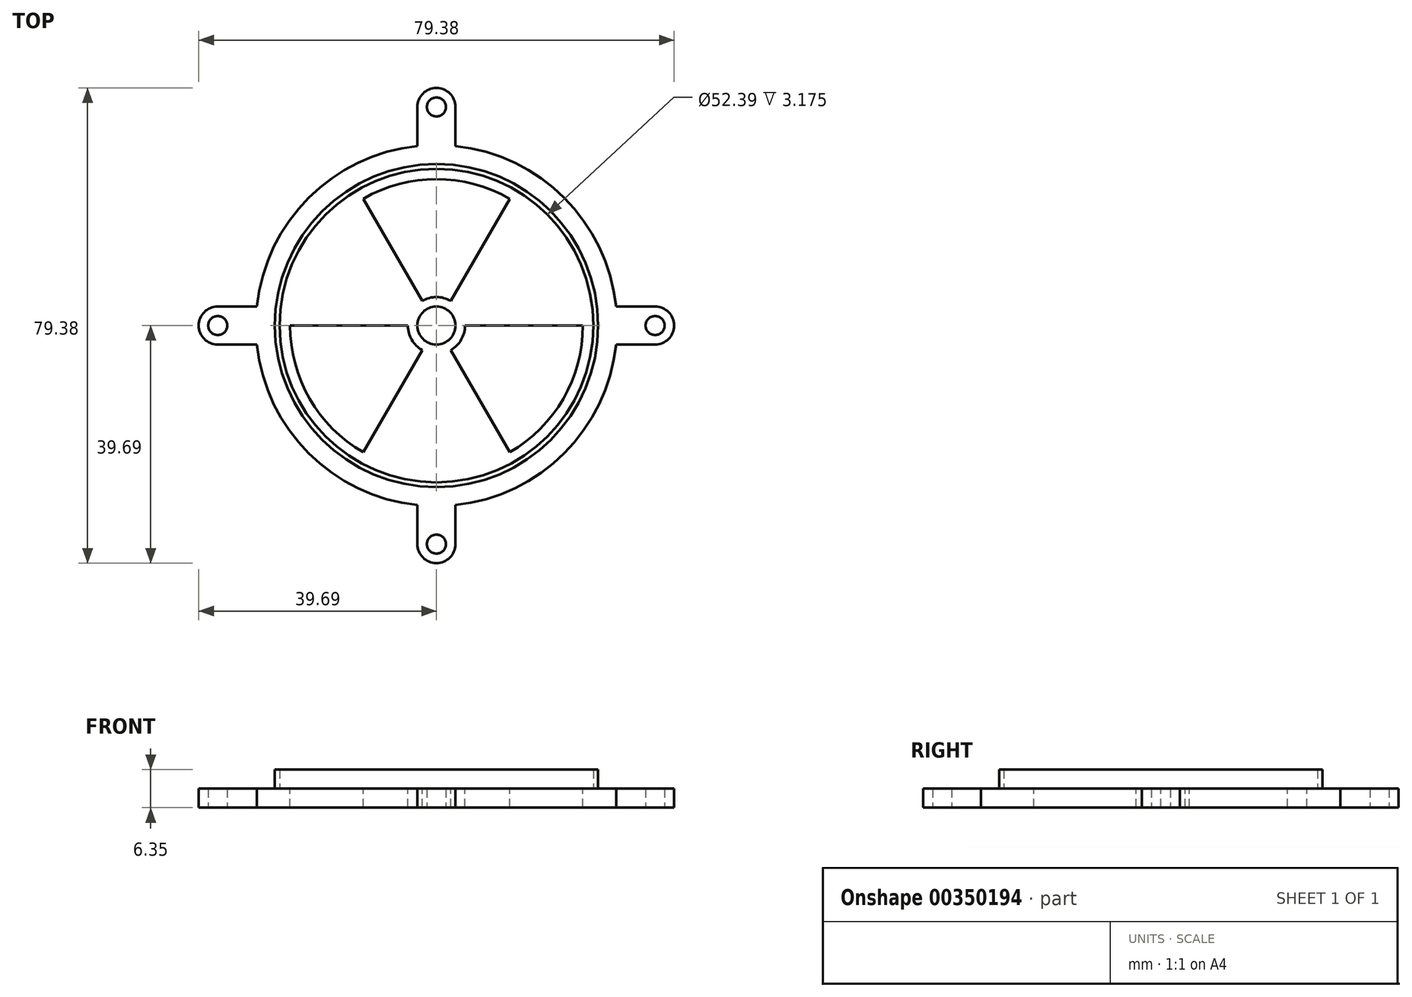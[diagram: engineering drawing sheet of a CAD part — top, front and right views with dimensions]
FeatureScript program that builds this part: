
annotation { "Feature Type Name" : "Feature", "Feature Type Description" : "" }
export const myFeature = defineFeature(function(context is Context, id is Id, definition is map)
    precondition{}
    {
        {
            var Q0;
            Q0=qCreatedBy(makeId("Top.planeOp"),FACE);
            var sketch = newSketch(context, id + "F0", { "sketchPlane" : qUnion([Q0])});
            skArc(sketch, "E0", {"start": v(30, 3.17) * mm, "mid": v(21.33, 21.33) * mm, "end": v(3.17, 30) * mm});
            skLineSegment(sketch, "E1.0", {"start": v(36.51, 3.18) * mm, "end": v(30, 3.17) * mm});
            skLineSegment(sketch, "E2.0", {"start": v(36.51, -3.17) * mm, "end": v(30, -3.17) * mm});
            skLineSegment(sketch, "E3.trimOffspring", {"start": v(-30, 3.17) * mm, "end": v(-30.16, 3.17) * mm});
            skArc(sketch, "E4", {"start": v(36.51, -3.17) * mm, "mid": v(39.69, 0) * mm, "end": v(36.51, 3.17) * mm});
            skCircle(sketch, "E5", {"center": v(36.51, 0) * mm, "radius": 1.59 * mm});
            skPoint(sketch, "E6.orphan", {"position": v(30.16, 0) * mm});
            skLineSegment(sketch, "E7.trimOffspring", {"start": v(-30, -3.18) * mm, "end": v(-30.16, -3.18) * mm});
            skLineSegment(sketch, "E8.1.0", {"start": v(-3.17, 36.51) * mm, "end": v(-3.17, 30) * mm});
            skArc(sketch, "E8.1.1", {"start": v(3.17, 36.51) * mm, "mid": v(0, 39.69) * mm, "end": v(-3.17, 36.51) * mm});
            skLineSegment(sketch, "E8.1.2", {"start": v(3.17, 36.51) * mm, "end": v(3.17, 30) * mm});
            skCircle(sketch, "E8.1.3", {"center": v(0, 36.51) * mm, "radius": 1.59 * mm});
            skLineSegment(sketch, "E8.2.0", {"start": v(-36.51, -3.17) * mm, "end": v(-30, -3.17) * mm});
            skArc(sketch, "E8.2.1", {"start": v(-36.51, 3.17) * mm, "mid": v(-39.69, 0) * mm, "end": v(-36.51, -3.17) * mm});
            skLineSegment(sketch, "E8.2.2", {"start": v(-36.51, 3.17) * mm, "end": v(-30, 3.17) * mm});
            skCircle(sketch, "E8.2.3", {"center": v(-36.51, 0) * mm, "radius": 1.59 * mm});
            skLineSegment(sketch, "E8.3.0", {"start": v(3.17, -36.51) * mm, "end": v(3.17, -30) * mm});
            skArc(sketch, "E8.3.1", {"start": v(-3.18, -36.51) * mm, "mid": v(0, -39.69) * mm, "end": v(3.17, -36.51) * mm});
            skLineSegment(sketch, "E8.3.2", {"start": v(-3.18, -36.51) * mm, "end": v(-3.18, -30) * mm});
            skCircle(sketch, "E8.3.3", {"center": v(0, -36.51) * mm, "radius": 1.59 * mm});
            skArc(sketch, "E9.trimOffspring", {"start": v(-3.17, 30) * mm, "mid": v(-21.33, 21.33) * mm, "end": v(-30, 3.17) * mm});
            skArc(sketch, "E10.trimOffspring", {"start": v(-30, -3.18) * mm, "mid": v(-21.33, -21.33) * mm, "end": v(-3.18, -30) * mm});
            skArc(sketch, "E11.trimOffspring", {"start": v(3.17, -30) * mm, "mid": v(21.33, -21.33) * mm, "end": v(30, -3.18) * mm});
            skSolve(sketch);
        }
        {
            var Q0;
            Q0=makeQuery(id+"F0.imprint","IMPRINT",FACE,{"disambiguationData":[TD([[makeQuery(id+"F0.imprint","IMPRINT",EDGE,{"derivedFrom":sQuery(id+"F0.wireOp",EDGE,"E0")}),1.0]])]});
            extrude(context, id + "F1", {"entities" : qUnion([Q0]), "depth" : 3.17 * mm});
        }
        {
            var Q0;
            Q0=makeQuery(id+"F1.opExtrude","CAP_FACE",FACE,{"disambiguationData":[OSD([sQuery(id+"F0.wireOp",EDGE,"E0"),sQuery(id+"F0.wireOp",EDGE,"E1.0"),sQuery(id+"F0.wireOp",EDGE,"E2.0"),sQuery(id+"F0.wireOp",EDGE,"E4"),sQuery(id+"F0.wireOp",EDGE,"E5"),sQuery(id+"F0.wireOp",EDGE,"E8.1.0"),sQuery(id+"F0.wireOp",EDGE,"E8.1.1"),sQuery(id+"F0.wireOp",EDGE,"E8.1.2"),sQuery(id+"F0.wireOp",EDGE,"E8.1.3"),sQuery(id+"F0.wireOp",EDGE,"E8.2.0"),sQuery(id+"F0.wireOp",EDGE,"E8.2.1"),sQuery(id+"F0.wireOp",EDGE,"E8.2.2"),sQuery(id+"F0.wireOp",EDGE,"E8.2.3"),sQuery(id+"F0.wireOp",EDGE,"E8.3.0"),sQuery(id+"F0.wireOp",EDGE,"E8.3.1"),sQuery(id+"F0.wireOp",EDGE,"E8.3.2"),sQuery(id+"F0.wireOp",EDGE,"E8.3.3"),sQuery(id+"F0.wireOp",EDGE,"E9.trimOffspring"),sQuery(id+"F0.wireOp",EDGE,"E10.trimOffspring"),sQuery(id+"F0.wireOp",EDGE,"E11.trimOffspring")])],"isStart":false});
            var sketch = newSketch(context, id + "F2", { "sketchPlane" : qUnion([Q0])});
            skCircle(sketch, "E12", {"center": v(0, 0) * mm, "radius": 26.99 * mm});
            skCircle(sketch, "E13", {"center": v(0, 0) * mm, "radius": 26.2 * mm});
            skSolve(sketch);
        }
        {
            var Q0;
            Q0=makeQuery(id+"F2.imprint","IMPRINT",FACE,{"disambiguationData":[TD([[makeQuery(id+"F2.imprint","IMPRINT",EDGE,{"derivedFrom":sQuery(id+"F2.wireOp",EDGE,"E12")}),1.0]])]});
            extrude(context, id + "F3", {"entities" : qUnion([Q0]), "operationType" : NewBodyOperationType.ADD, "depth" : 3.17 * mm});
        }
        {
            var Q0;
            Q0=makeQuery(id+"F3.boolean.opBoolean","SPLIT",FACE,{"disambiguationData":[TD([makeQuery(id+"F3.opExtrude","SWEPT_FACE",FACE,{"disambiguationData":[OSD([sQuery(id+"F2.wireOp",EDGE,"E13")])]})])],"derivedFrom":makeQuery(id+"F1.opExtrude","CAP_FACE",FACE,{"disambiguationData":[OSD([sQuery(id+"F0.wireOp",EDGE,"E0"),sQuery(id+"F0.wireOp",EDGE,"E1.0"),sQuery(id+"F0.wireOp",EDGE,"E2.0"),sQuery(id+"F0.wireOp",EDGE,"E4"),sQuery(id+"F0.wireOp",EDGE,"E5"),sQuery(id+"F0.wireOp",EDGE,"E8.1.0"),sQuery(id+"F0.wireOp",EDGE,"E8.1.1"),sQuery(id+"F0.wireOp",EDGE,"E8.1.2"),sQuery(id+"F0.wireOp",EDGE,"E8.1.3"),sQuery(id+"F0.wireOp",EDGE,"E8.2.0"),sQuery(id+"F0.wireOp",EDGE,"E8.2.1"),sQuery(id+"F0.wireOp",EDGE,"E8.2.2"),sQuery(id+"F0.wireOp",EDGE,"E8.2.3"),sQuery(id+"F0.wireOp",EDGE,"E8.3.0"),sQuery(id+"F0.wireOp",EDGE,"E8.3.1"),sQuery(id+"F0.wireOp",EDGE,"E8.3.2"),sQuery(id+"F0.wireOp",EDGE,"E8.3.3"),sQuery(id+"F0.wireOp",EDGE,"E9.trimOffspring"),sQuery(id+"F0.wireOp",EDGE,"E10.trimOffspring"),sQuery(id+"F0.wireOp",EDGE,"E11.trimOffspring")])],"isStart":false})});
            var sketch = newSketch(context, id + "F4", { "sketchPlane" : qUnion([Q0])});
            skCircle(sketch, "E14", {"center": v(0, 0) * mm, "radius": 3.18 * mm});
            skArc(sketch, "E15", {"start": v(2.38, 4.12) * mm, "mid": v(0, 4.76) * mm, "end": v(-2.38, 4.12) * mm});
            skArc(sketch, "E16", {"start": v(-24.45, 0) * mm, "mid": v(-21.17, -12.22) * mm, "end": v(-12.22, -21.17) * mm});
            skLineSegment(sketch, "E17.1.0", {"start": v(-2.38, 4.12) * mm, "end": v(-12.22, 21.17) * mm});
            skLineSegment(sketch, "E17.3.0", {"start": v(-4.76, 0) * mm, "end": v(-24.45, 0) * mm});
            skLineSegment(sketch, "E18.2.7.0", {"start": v(2.38, -4.12) * mm, "end": v(12.22, -21.17) * mm});
            skLineSegment(sketch, "E18.2.9.0", {"start": v(4.76, 0) * mm, "end": v(24.45, 0) * mm});
            skLineSegment(sketch, "E18.2.11.0", {"start": v(2.38, 4.12) * mm, "end": v(12.22, 21.17) * mm});
            skLineSegment(sketch, "E19.trimOffspring", {"start": v(-2.38, -4.12) * mm, "end": v(-12.22, -21.17) * mm});
            skArc(sketch, "E20.trimOffspring", {"start": v(2.38, -4.12) * mm, "mid": v(4.12, -2.38) * mm, "end": v(4.76, 0) * mm});
            skArc(sketch, "E21.trimOffspring", {"start": v(-4.76, 0) * mm, "mid": v(-4.12, -2.38) * mm, "end": v(-2.38, -4.12) * mm});
            skArc(sketch, "E22.trimOffspring", {"start": v(12.22, -21.17) * mm, "mid": v(21.17, -12.22) * mm, "end": v(24.45, 0) * mm});
            skArc(sketch, "E23.trimOffspring", {"start": v(12.22, 21.17) * mm, "mid": v(0, 24.45) * mm, "end": v(-12.22, 21.17) * mm});
            skSolve(sketch);
        }
        {
            var Q0;
            Q0=makeQuery(id+"F4.imprint","IMPRINT",FACE,{"disambiguationData":[TD([[makeQuery(id+"F4.imprint","IMPRINT",EDGE,{"derivedFrom":sQuery(id+"F4.wireOp",EDGE,"E15")}),-1.0]])]});
            var Q1;
            Q1=makeQuery(id+"F4.imprint","IMPRINT",FACE,{"disambiguationData":[TD([[makeQuery(id+"F4.imprint","IMPRINT",EDGE,{"derivedFrom":sQuery(id+"F4.wireOp",EDGE,"E14")}),1.0]])]});
            var Q2;
            Q2=makeQuery(id+"F4.imprint","IMPRINT",FACE,{"disambiguationData":[TD([[makeQuery(id+"F4.imprint","IMPRINT",EDGE,{"derivedFrom":sQuery(id+"F4.wireOp",EDGE,"E18.2.7.0")}),1.0]])]});
            var Q3;
            Q3=makeQuery(id+"F4.imprint","IMPRINT",FACE,{"disambiguationData":[TD([[makeQuery(id+"F4.imprint","IMPRINT",EDGE,{"derivedFrom":sQuery(id+"F4.wireOp",EDGE,"E16")}),1.0]])]});
            extrude(context, id + "F5", {"entities" : qUnion([Q0, Q1, Q2, Q3]), "operationType" : NewBodyOperationType.REMOVE, "oppositeDirection" : true, "depth" : 3.17 * mm});
        }
    });
